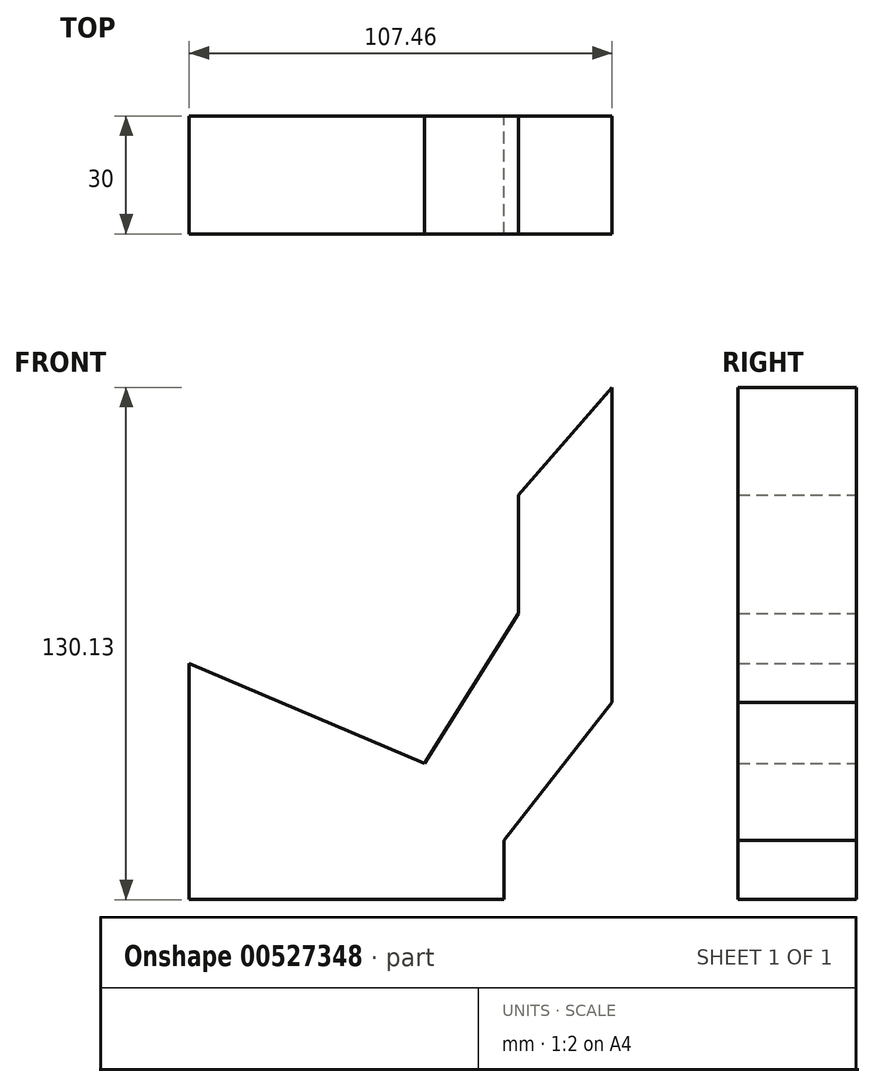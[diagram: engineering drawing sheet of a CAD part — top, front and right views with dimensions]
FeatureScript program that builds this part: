
annotation { "Feature Type Name" : "Feature", "Feature Type Description" : "" }
export const myFeature = defineFeature(function(context is Context, id is Id, definition is map)
    precondition{}
    {
        {
            var Q0;
            Q0=qCreatedBy(makeId("Front.planeOp"),FACE);
            var sketch = newSketch(context, id + "F0", { "sketchPlane" : qUnion([Q0])});
            skLineSegment(sketch, "E0", {"start": v(-48.47, -3.05) * mm, "end": v(-48.47, -63.05) * mm});
            skLineSegment(sketch, "E1", {"start": v(-48.47, -63.05) * mm, "end": v(31.53, -63.05) * mm});
            skLineSegment(sketch, "E2", {"start": v(-48.47, -3.05) * mm, "end": v(11.36, -28.44) * mm});
            skLineSegment(sketch, "E3", {"start": v(31.53, -63.05) * mm, "end": v(31.53, -48.05) * mm});
            skLineSegment(sketch, "E4", {"start": v(11.36, -28.44) * mm, "end": v(35.2, 9.72) * mm});
            skLineSegment(sketch, "E5", {"start": v(35.2, 9.72) * mm, "end": v(35.2, 39.72) * mm});
            skLineSegment(sketch, "E6", {"start": v(35.2, 39.72) * mm, "end": v(59, 67.08) * mm});
            skLineSegment(sketch, "E7", {"start": v(59, 67.08) * mm, "end": v(59, -12.92) * mm});
            skLineSegment(sketch, "E8", {"start": v(31.53, -48.05) * mm, "end": v(59, -12.92) * mm});
            skSolve(sketch);
        }
        {
            var Q0;
            Q0=makeQuery(id+"F0.imprint","IMPRINT",FACE,{"disambiguationData":[TD([[makeQuery(id+"F0.imprint","IMPRINT",EDGE,{"derivedFrom":sQuery(id+"F0.wireOp",EDGE,"E0")}),1.0]])]});
            extrude(context, id + "F1", {"entities" : qUnion([Q0]), "depth" : 30 * mm, "offsetDistance" : 25 * mm});
        }
    });
